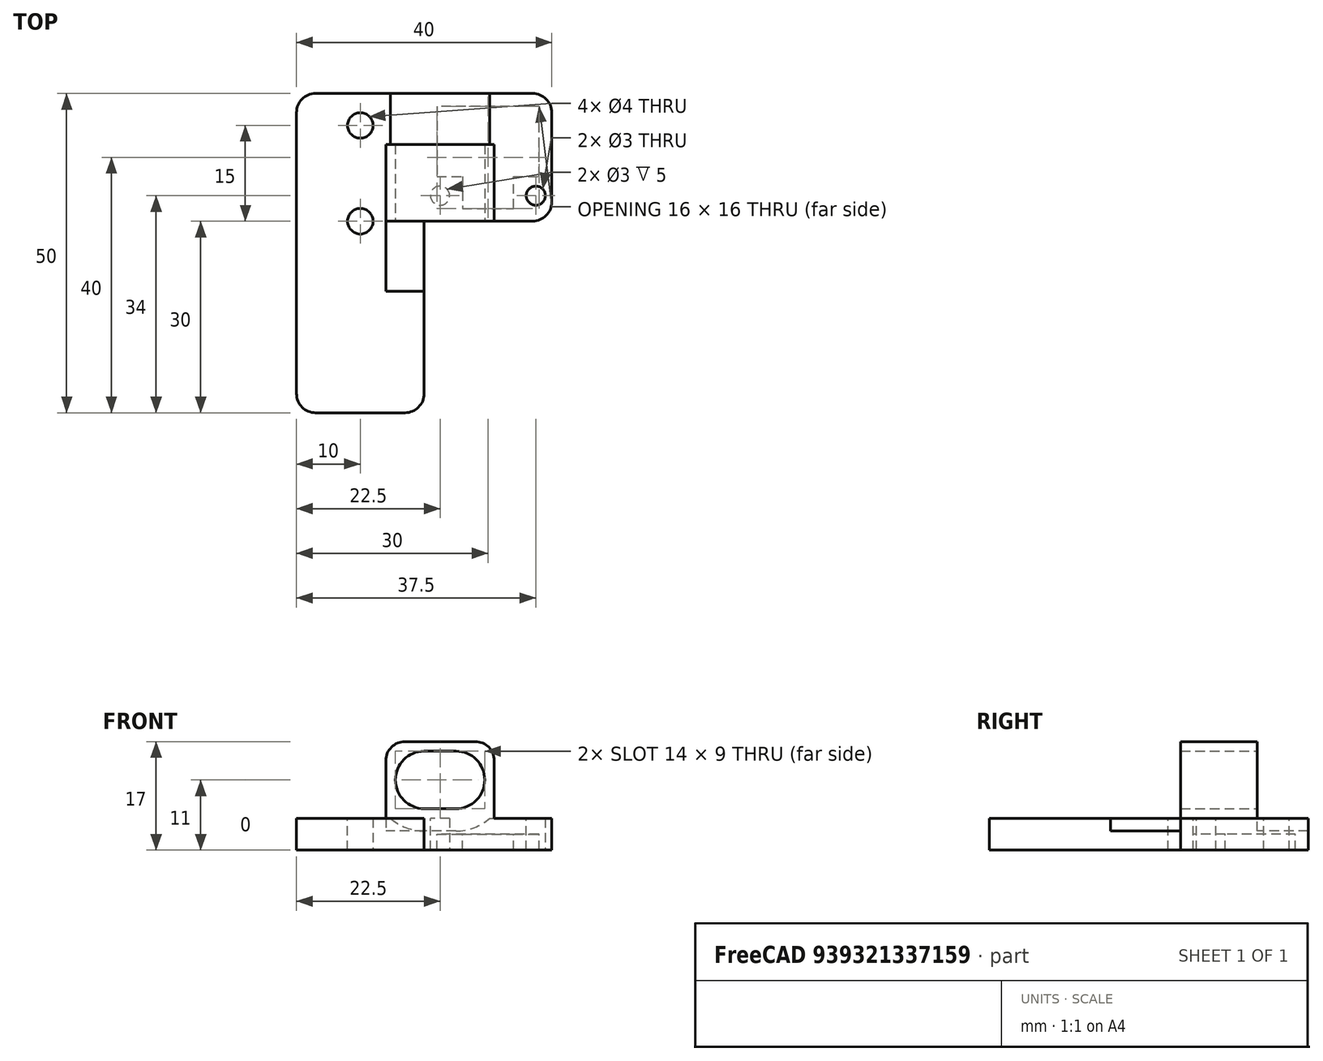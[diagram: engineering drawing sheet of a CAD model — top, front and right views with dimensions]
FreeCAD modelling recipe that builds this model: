
FCSTD DOCUMENT  (FreeCAD 0.19R24291 (Git))
Label: Inductive Endstop v2
License: All rights reserved
LicenseURL: http://en.wikipedia.org/wiki/All_rights_reserved
objects: Sketcher::SketchObject×10, PartDesign::Pocket×8, PartDesign::Pad×2, PartDesign::Fillet×1, PartDesign::Body×1, Part::Refine×1, Mesh::Feature×1
note: 34 computed .brp shape members not serialized (recipe doc carries the construction recipe); baked Part::Feature solids carry a one-line shape summary decoded from their .brp

FEATURE [Sketcher::SketchObject] Sketch
  FullyConstrained = true
  MapMode = 5
  Support = -> [XY_Plane]
  sketch-geometry (6):
    g0: LineSegment StartX=-20 StartY=20 StartZ=0 EndX=20 EndY=20 EndZ=0
    g1: LineSegment StartX=20 StartY=20 StartZ=0 EndX=20 EndY=0 EndZ=0
    g2: LineSegment StartX=20 StartY=0 StartZ=0 EndX=0 EndY=0 EndZ=0
    g3: LineSegment StartX=0 StartY=0 StartZ=0 EndX=0 EndY=-30 EndZ=0
    g4: LineSegment StartX=0 StartY=-30 StartZ=0 EndX=-20 EndY=-30 EndZ=0
    g5: LineSegment StartX=-20 StartY=-30 StartZ=0 EndX=-20 EndY=20 EndZ=0
  constraints (17):
    c: Horizontal(g0)
    c: Coincident(g0,g1)
    c: Coincident(g1,g2)
    c: Coincident(g2,g3)
    c: Coincident(g3,g4)
    c: Coincident(g4,g5)
    c: Vertical(g5)
    c: Coincident(g0,g5)
    c: Parallel(g5,g1)
    c: Parallel(g0,g2)
    c: Parallel(g2,g4)
    c: Parallel(g3,g5)
    c: DistanceY(g5,g5) = 50
    c: DistanceX(g0,g0) = 40
    c: DistanceX(g2,g2) = 20
    c: DistanceY(g1,g1) = 20
    c: Coincident(g2,g-1)
FEATURE [PartDesign::Pad] Pad
  Direction = (1,1,1)
  Length = 5
  Length2 = 100
  Profile = -> Sketch
  Type = 0
FEATURE [Sketcher::SketchObject] Sketch001
  FullyConstrained = true
  MapMode = 5
  Placement = pos=(0,0,5) rot=(0,0,1;0rad)
  Support = -> [Pad]
  sketch-geometry (1):
    g0: Circle CenterX=-10 CenterY=15 CenterZ=0 NormalX=0 NormalY=0 NormalZ=1 AngleXU=0 Radius=2
  constraints (3):
    c: DistanceX(g0) = -10
    c: DistanceY(g0) = 15
    c: Diameter(g0) = 4
FEATURE [PartDesign::Pocket] Pocket
  BaseFeature = -> Pad
  Length = 5
  Length2 = 100
  Profile = -> Sketch001
  Type = 1
FEATURE [Sketcher::SketchObject] Sketch002
  FullyConstrained = true
  MapMode = 5
  Placement = pos=(0,0,5) rot=(0,0,1;0rad)
  Support = -> [Pocket]
  sketch-geometry (1):
    g0: Circle CenterX=-10 CenterY=0 CenterZ=0 NormalX=0 NormalY=0 NormalZ=1 AngleXU=0 Radius=2
  constraints (3):
    c: Diameter(g0) = 4
    c: DistanceX(g0) = -10
    c: DistanceY(g0) = 0
FEATURE [PartDesign::Pocket] Pocket001
  BaseFeature = -> Pocket
  Length = 5
  Length2 = 100
  Profile = -> Sketch002
  Type = 1
FEATURE [Sketcher::SketchObject] Sketch003
  FullyConstrained = true
  MapMode = 5
  Placement = pos=(0,0,5) rot=(0,0,1;0rad)
  Support = -> [Pocket001]
  sketch-geometry (1):
    g0: Circle CenterX=2.5 CenterY=4 CenterZ=0 NormalX=0 NormalY=0 NormalZ=1 AngleXU=0 Radius=1.5
  constraints (3):
    c: Diameter(g0) = 3
    c: DistanceY(g0) = 4
    c: DistanceX(g0) = 2.5
FEATURE [PartDesign::Pocket] Pocket002
  BaseFeature = -> Pocket001
  Length = 5
  Length2 = 100
  Profile = -> Sketch003
  Type = 1
FEATURE [Sketcher::SketchObject] Sketch004
  FullyConstrained = true
  MapMode = 5
  Placement = pos=(0,0,5) rot=(0,0,1;0rad)
  Support = -> [Pocket002]
  sketch-geometry (1):
    g0: Circle CenterX=17.5 CenterY=4 CenterZ=0 NormalX=0 NormalY=0 NormalZ=1 AngleXU=0 Radius=1.5
  constraints (3):
    c: Diameter(g0) = 3
    c: DistanceY(g0) = 4
    c: DistanceX(g0) = 17.5
FEATURE [PartDesign::Pocket] Pocket003
  BaseFeature = -> Pocket002
  Length = 5
  Length2 = 100
  Profile = -> Sketch004
  Type = 1
FEATURE [Sketcher::SketchObject] Sketch005
  FullyConstrained = true
  MapMode = 5
  Placement = pos=(0,0,5) rot=(0,0,1;0rad)
  Support = -> [Pocket003]
  sketch-geometry (4):
    g0: LineSegment StartX=-6 StartY=12 StartZ=0 EndX=11 EndY=12 EndZ=0
    g1: LineSegment StartX=11 StartY=12 StartZ=0 EndX=11 EndY=0 EndZ=0
    g2: LineSegment StartX=11 StartY=0 StartZ=0 EndX=-6 EndY=0 EndZ=0
    g3: LineSegment StartX=-6 StartY=0 StartZ=0 EndX=-6 EndY=12 EndZ=0
  constraints (12):
    c: Coincident(g0,g1)
    c: Coincident(g1,g2)
    c: Coincident(g2,g3)
    c: Coincident(g3,g0)
    c: Horizontal(g0)
    c: Horizontal(g2)
    c: Vertical(g1)
    c: Vertical(g3)
    c: DistanceY(g1,g1) = 12
    c: DistanceX(g0,g0) = 17
    c: DistanceX(g2) = -6
    c: PointOnObject(g2,g-1)
FEATURE [PartDesign::Pad] Pad001  label="Sensor mount"
  BaseFeature = -> Pocket003
  Direction = (1,1,1)
  Length = 12
  Length2 = 100
  Profile = -> Sketch005
  Type = 0
FEATURE [Sketcher::SketchObject] Sketch009  label="PCB pocket"
  FullyConstrained = true
  MapMode = 5
  Placement = pos=(0,0,0) rot=(1,0,0;3.14159rad)
  sketch-geometry (8):
    g0: LineSegment StartX=6 StartY=-2 StartZ=0 EndX=14 EndY=-2 EndZ=0
    g1: LineSegment StartX=14 StartY=-2 StartZ=0 EndX=14 EndY=-7 EndZ=0
    g2: LineSegment StartX=14 StartY=-7 StartZ=0 EndX=18 EndY=-7 EndZ=0
    g3: LineSegment StartX=18 StartY=-7 StartZ=0 EndX=18 EndY=-18 EndZ=0
    g4: LineSegment StartX=18 StartY=-18 StartZ=0 EndX=2 EndY=-18 EndZ=0
    g5: LineSegment StartX=2 StartY=-18 StartZ=0 EndX=2 EndY=-7 EndZ=0
    g6: LineSegment StartX=2 StartY=-7 StartZ=0 EndX=6 EndY=-7 EndZ=0
    g7: LineSegment StartX=6 StartY=-7 StartZ=0 EndX=6 EndY=-2 EndZ=0
  constraints (21):
    c: Horizontal(g0)
    c: Coincident(g0,g1)
    c: Coincident(g1,g2)
    c: Coincident(g2,g3)
    c: Coincident(g3,g4)
    c: Horizontal(g4)
    c: Coincident(g4,g5)
    c: Coincident(g5,g6)
    c: Coincident(g6,g7)
    c: Coincident(g7,g0)
    c: DistanceX(g5) = 2
    c: DistanceY(g5) = -7
    c: DistanceX(g1) = 14
    c: DistanceY(g1) = -7
    c: DistanceX(g0) = 6
    c: DistanceY(g0) = -2
    c: Block(g5)
    c: Block(g4)
    c: Block(g3)
    c: Block(g7)
    c: Block(g0)
FEATURE [Sketcher::SketchObject] Sketch010  label="Sensor hole"
  FullyConstrained = true
  MapMode = 5
  Placement = pos=(0,0,0) rot=(1,0,0;1.5708rad)
  Support = -> [Pad001]
  sketch-geometry (4):
    g0: ArcOfCircle CenterX=0 CenterY=11 CenterZ=0 NormalX=0 NormalY=0 NormalZ=1 AngleXU=0 Radius=4.5 StartAngle=1.5708 EndAngle=4.71239
    g1: ArcOfCircle CenterX=5 CenterY=11 CenterZ=0 NormalX=0 NormalY=0 NormalZ=1 AngleXU=0 Radius=4.5 StartAngle=4.71239 EndAngle=7.85398
    g2: LineSegment StartX=-8e-16 StartY=6.5 StartZ=0 EndX=5 EndY=6.5 EndZ=0
    g3: LineSegment StartX=-7e-16 StartY=15.5 StartZ=0 EndX=5 EndY=15.5 EndZ=0
  constraints (10):
    c: Tangent(g0,g3) = 1.5708
    c: Tangent(g0,g2) = -1.5708
    c: Tangent(g2,g1) = -1.5708
    c: Tangent(g3,g1) = 1.5708
    c: Horizontal(g2)
    c: Equal(g0,g1)
    c: PointOnObject(g0,g-2)
    c: Radius(g1) = 4.5
    c: DistanceX(g3,g3) = 5
    c: DistanceY(g0) = 11
FEATURE [PartDesign::Pocket] Pocket004
  BaseFeature = -> Pad001
  Length = 5
  Length2 = 100
  Profile = -> Sketch010
  Type = 1
FEATURE [Sketcher::SketchObject] Sketch011
  FullyConstrained = true
  MapMode = 5
  Placement = pos=(0,20,0) rot=(0,0.707107,0.707107;3.14159rad)
  Support = -> [Pocket004]
  sketch-geometry (4):
    g0: ArcOfCircle CenterX=-5 CenterY=11 CenterZ=0 NormalX=0 NormalY=0 NormalZ=1 AngleXU=0 Radius=8 StartAngle=1.5708 EndAngle=4.71239
    g1: ArcOfCircle CenterX=0 CenterY=11 CenterZ=0 NormalX=0 NormalY=0 NormalZ=1 AngleXU=0 Radius=8 StartAngle=4.71239 EndAngle=7.85398
    g2: LineSegment StartX=-5 StartY=3 StartZ=0 EndX=-1.8e-15 EndY=3 EndZ=0
    g3: LineSegment StartX=-5 StartY=19 StartZ=0 EndX=2.7e-15 EndY=19 EndZ=0
  constraints (10):
    c: Tangent(g0,g3) = 1.5708
    c: Tangent(g0,g2) = -1.5708
    c: Tangent(g2,g1) = -1.5708
    c: Tangent(g3,g1) = 1.5708
    c: Horizontal(g2)
    c: Equal(g0,g1)
    c: Radius(g0) = 8
    c: DistanceX(g2,g2) = 5
    c: PointOnObject(g1,g-2)
    c: DistanceY(g1) = 11
FEATURE [PartDesign::Pocket] Pocket005
  BaseFeature = -> Pocket004
  Length = 8
  Length2 = 100
  Profile = -> Sketch011
  Type = 0
FEATURE [Sketcher::SketchObject] Sketch012
  FullyConstrained = true
  MapMode = 5
  Placement = pos=(0,0,5) rot=(0,0,1;0rad)
  Support = -> [Pocket005]
  sketch-geometry (4):
    g0: LineSegment StartX=-6 StartY=0 StartZ=0 EndX=0 EndY=0 EndZ=0
    g1: LineSegment StartX=0 StartY=0 StartZ=0 EndX=0 EndY=-11 EndZ=0
    g2: LineSegment StartX=0 StartY=-11 StartZ=0 EndX=-6 EndY=-11 EndZ=0
    g3: LineSegment StartX=-6 StartY=-11 StartZ=0 EndX=-6 EndY=0 EndZ=0
  constraints (12):
    c: Coincident(g0,g1)
    c: Coincident(g1,g2)
    c: Coincident(g2,g3)
    c: Coincident(g3,g0)
    c: Horizontal(g0)
    c: Horizontal(g2)
    c: Vertical(g1)
    c: Vertical(g3)
    c: PointOnObject(g0,g-1)
    c: PointOnObject(g1,g-2)
    c: DistanceX(g2) = -6
    c: DistanceY(g2) = -11
FEATURE [PartDesign::Pocket] Pocket006
  BaseFeature = -> Pocket005
  Length = 2
  Length2 = 100
  Profile = -> Sketch012
  Type = 0
FEATURE [PartDesign::Pocket] Pocket007
  BaseFeature = -> Pocket006
  Length = 2.5
  Length2 = 100
  Profile = -> Sketch009
  Type = 0
FEATURE [PartDesign::Fillet] Fillet
  Base = -> Pocket007 [Edge8,Edge81,Edge91,Edge2,Edge26,Edge49,Edge48]
  BaseFeature = -> Pocket007
  Radius = 3
  SupportTransform = false
FEATURE [PartDesign::Body] Body
  Group = -> [Sketch,Pad,Sketch001,Pocket,Sketch002,Pocket001,Sketch003,Pocket002,Sketch004,Pocket003,Sketch005,Pad001,Sketch009,Sketch010,Pocket004,Sketch011,Pocket005,Sketch012,Pocket006,Pocket007,Fillet]
  Origin = -> Origin
  Tip = -> Fillet
FEATURE [Part::Refine] Fillet001
  Source = -> Fillet
FEATURE [Mesh::Feature] dummy
  Placement = pos=(0,-18,11) rot=(1,0,0;4.71239rad)
